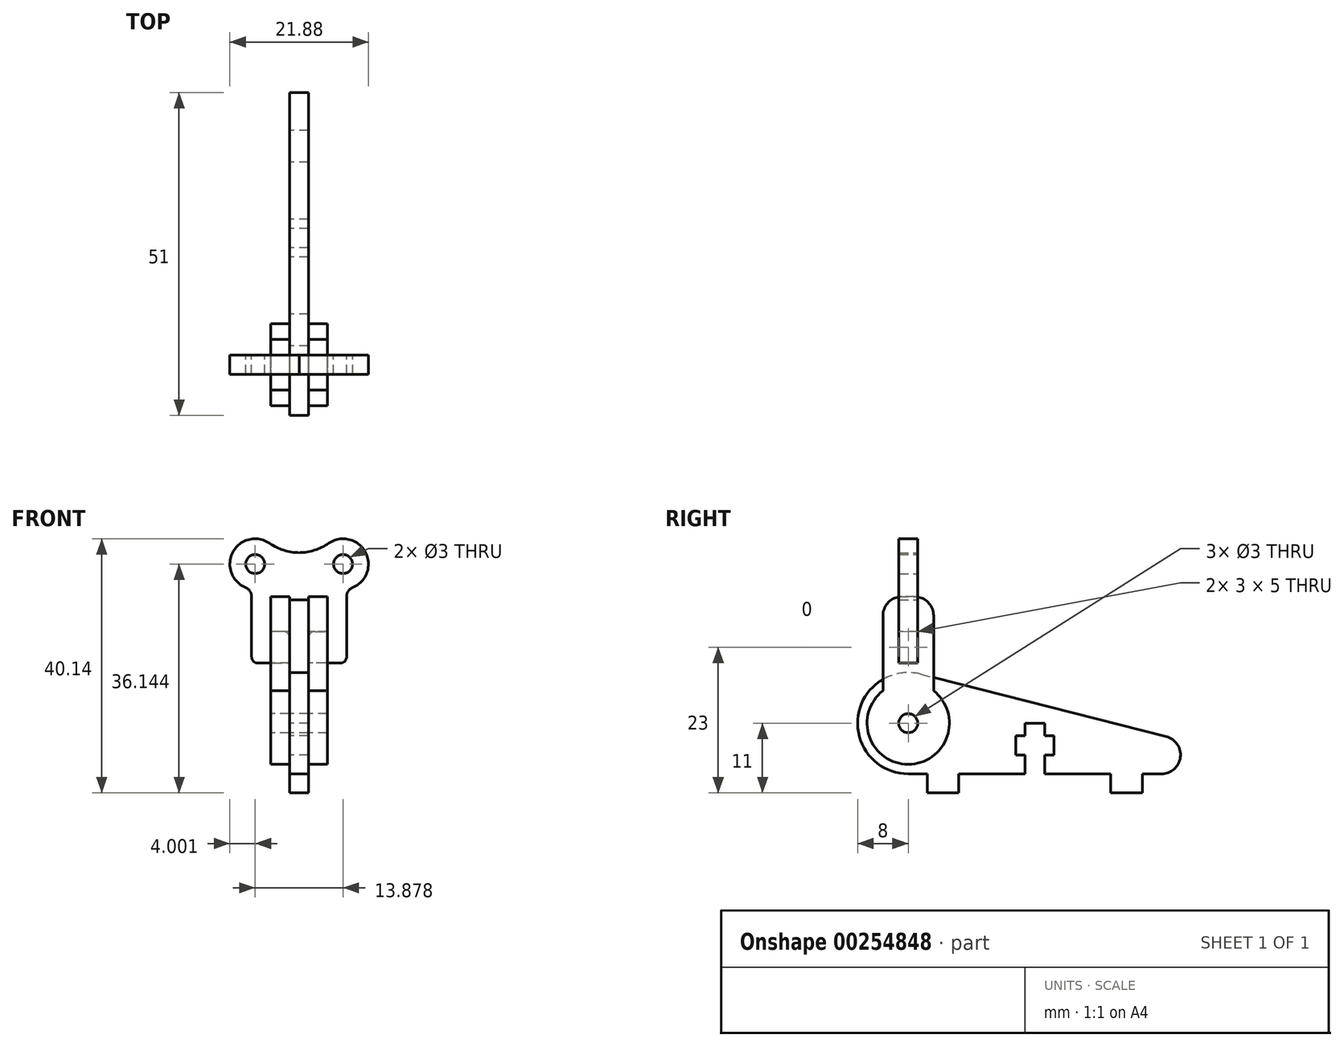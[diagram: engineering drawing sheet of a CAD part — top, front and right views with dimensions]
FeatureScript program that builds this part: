
annotation { "Feature Type Name" : "Feature", "Feature Type Description" : "" }
export const myFeature = defineFeature(function(context is Context, id is Id, definition is map)
    precondition{}
    {
        {
            var Q0;
            Q0=qCreatedBy(makeId("Right.planeOp"),FACE);
            var sketch = newSketch(context, id + "F0", { "sketchPlane" : qUnion([Q0])});
            skLineSegment(sketch, "E0", {"start": v(-20, 0) * mm, "end": v(-17, 0) * mm});
            skLineSegment(sketch, "E1", {"start": v(-17, 0) * mm, "end": v(-17, -3) * mm});
            skLineSegment(sketch, "E2", {"start": v(-17, -3) * mm, "end": v(-12, -3) * mm});
            skLineSegment(sketch, "E3", {"start": v(-12, -3) * mm, "end": v(-12, 0) * mm});
            skLineSegment(sketch, "E4", {"start": v(-12, 0) * mm, "end": v(-1.55, 0) * mm});
            skLineSegment(sketch, "E5", {"start": v(1.55, 0) * mm, "end": v(12, 0) * mm});
            skLineSegment(sketch, "E6", {"start": v(12, 0) * mm, "end": v(12, -3) * mm});
            skLineSegment(sketch, "E7", {"start": v(12, -3) * mm, "end": v(17, -3) * mm});
            skLineSegment(sketch, "E8", {"start": v(17, -3) * mm, "end": v(17, 0) * mm});
            skLineSegment(sketch, "E9", {"start": v(17, 0) * mm, "end": v(20, 0) * mm});
            skLineSegment(sketch, "E10", {"start": v(-1.55, 0) * mm, "end": v(-1.55, 3) * mm});
            skLineSegment(sketch, "E11", {"start": v(-1.55, 3) * mm, "end": v(-3, 3) * mm});
            skLineSegment(sketch, "E12", {"start": v(-3, 3) * mm, "end": v(-3, 6) * mm});
            skLineSegment(sketch, "E13", {"start": v(-3, 6) * mm, "end": v(-1.55, 6) * mm});
            skLineSegment(sketch, "E14", {"start": v(-1.55, 6) * mm, "end": v(-1.55, 8) * mm});
            skLineSegment(sketch, "E15", {"start": v(-1.55, 8) * mm, "end": v(1.55, 8) * mm});
            skLineSegment(sketch, "E16", {"start": v(1.55, 8) * mm, "end": v(1.55, 6) * mm});
            skLineSegment(sketch, "E17", {"start": v(1.55, 6) * mm, "end": v(3, 6) * mm});
            skLineSegment(sketch, "E18", {"start": v(3, 6) * mm, "end": v(3, 3) * mm});
            skLineSegment(sketch, "E19", {"start": v(3, 3) * mm, "end": v(1.55, 3) * mm});
            skLineSegment(sketch, "E20", {"start": v(1.55, 0) * mm, "end": v(1.55, 3) * mm});
            skArc(sketch, "E21", {"start": v(-20, 0) * mm, "mid": v(-27.94, 9) * mm, "end": v(-18.03, 15.75) * mm});
            skCircle(sketch, "E22", {"center": v(-20, 8) * mm, "radius": 1.5 * mm});
            skArc(sketch, "E23", {"start": v(20, 0) * mm, "mid": v(22.98, 2.63) * mm, "end": v(20.74, 5.9) * mm});
            skLineSegment(sketch, "E24", {"start": v(-18.03, 15.75) * mm, "end": v(20.74, 5.9) * mm});
            skSolve(sketch);
        }
        {
            var Q0;
            Q0 = qSketchRegion(id + "F0", true);
            extrude(context, id + "F1", {"entities" : qUnion([Q0]), "depth" : 3 * mm, "symmetric" : true});
        }
        {
            var Q0;
            Q0=makeQuery(id+"F1.opExtrude","CAP_FACE",FACE,{"disambiguationData":[OSD([sQuery(id+"F0.wireOp",EDGE,"E0"),sQuery(id+"F0.wireOp",EDGE,"E1"),sQuery(id+"F0.wireOp",EDGE,"E2"),sQuery(id+"F0.wireOp",EDGE,"E3"),sQuery(id+"F0.wireOp",EDGE,"E4"),sQuery(id+"F0.wireOp",EDGE,"E5"),sQuery(id+"F0.wireOp",EDGE,"E6"),sQuery(id+"F0.wireOp",EDGE,"E7"),sQuery(id+"F0.wireOp",EDGE,"E8"),sQuery(id+"F0.wireOp",EDGE,"E9"),sQuery(id+"F0.wireOp",EDGE,"E10"),sQuery(id+"F0.wireOp",EDGE,"E11"),sQuery(id+"F0.wireOp",EDGE,"E12"),sQuery(id+"F0.wireOp",EDGE,"E13"),sQuery(id+"F0.wireOp",EDGE,"E14"),sQuery(id+"F0.wireOp",EDGE,"E15"),sQuery(id+"F0.wireOp",EDGE,"E16"),sQuery(id+"F0.wireOp",EDGE,"E17"),sQuery(id+"F0.wireOp",EDGE,"E18"),sQuery(id+"F0.wireOp",EDGE,"E19"),sQuery(id+"F0.wireOp",EDGE,"E20"),sQuery(id+"F0.wireOp",EDGE,"E21"),sQuery(id+"F0.wireOp",EDGE,"E22"),sQuery(id+"F0.wireOp",EDGE,"E23"),sQuery(id+"F0.wireOp",EDGE,"E24")])],"isStart":false});
            var sketch = newSketch(context, id + "F2", { "sketchPlane" : qUnion([Q0])});
            skCircle(sketch, "E25", {"center": v(-20, 8) * mm, "radius": 1.5 * mm});
            skArc(sketch, "E26.0", {"start": v(-24, 13.12) * mm, "mid": v(-20, 1.5) * mm, "end": v(-16, 13.12) * mm});
            skLineSegment(sketch, "E27", {"start": v(-20, 24.79) * mm, "end": v(-20, -12.76) * mm, "construction": true});
            skLineSegment(sketch, "E28.top", {"start": v(-19, 28) * mm, "end": v(-21, 28) * mm});
            skLineSegment(sketch, "E28.left", {"start": v(-16, 13.12) * mm, "end": v(-16, 25) * mm});
            skLineSegment(sketch, "E28.right", {"start": v(-24, 13.12) * mm, "end": v(-24, 25) * mm});
            skPoint(sketch, "E28.middle", {"position": v(-20, 20.56) * mm});
            skLineSegment(sketch, "E29.bottom", {"start": v(-18.5, 17.5) * mm, "end": v(-21.5, 17.5) * mm});
            skLineSegment(sketch, "E29.top", {"start": v(-18.5, 22.5) * mm, "end": v(-21.5, 22.5) * mm});
            skLineSegment(sketch, "E29.left", {"start": v(-18.5, 17.5) * mm, "end": v(-18.5, 22.5) * mm});
            skLineSegment(sketch, "E29.right", {"start": v(-21.5, 17.5) * mm, "end": v(-21.5, 22.5) * mm});
            skPoint(sketch, "E29.middle", {"position": v(-20, 20) * mm});
            skPoint(sketch, "E30.visualSharp", {"position": v(-24, 28) * mm});
            skArc(sketch, "E30.filletArc", {"start": v(-21, 28) * mm, "mid": v(-23.12, 27.12) * mm, "end": v(-24, 25) * mm});
            skPoint(sketch, "E31.visualSharp", {"position": v(-16, 28) * mm});
            skArc(sketch, "E31.filletArc", {"start": v(-16, 25) * mm, "mid": v(-16.88, 27.12) * mm, "end": v(-19, 28) * mm});
            skSolve(sketch);
        }
        {
            var Q0;
            Q0 = qSketchRegion(id + "F2", true);
            extrude(context, id + "F3", {"entities" : qUnion([Q0]), "depth" : 3 * mm});
        }
        {
            var Q0;
            Q0=makeQuery(id+"F3.opExtrude","SWEPT_BODY",BODY,{"disambiguationData":[OSD([sQuery(id+"F2.wireOp",EDGE,"E25"),sQuery(id+"F2.wireOp",EDGE,"E26.0"),sQuery(id+"F2.wireOp",EDGE,"E28.top"),sQuery(id+"F2.wireOp",EDGE,"E28.left"),sQuery(id+"F2.wireOp",EDGE,"E28.right"),sQuery(id+"F2.wireOp",EDGE,"E29.bottom"),sQuery(id+"F2.wireOp",EDGE,"E29.top"),sQuery(id+"F2.wireOp",EDGE,"E29.left"),sQuery(id+"F2.wireOp",EDGE,"E29.right"),sQuery(id+"F2.wireOp",EDGE,"E30.filletArc"),sQuery(id+"F2.wireOp",EDGE,"E31.filletArc")])]});
            transform(context, id + "F4", {"entities" : qUnion([Q0]), "transformType" : TransformType.TRANSLATION_3D, "dx" : -6 * mm, "dy" : 0 * mm, "dz" : 0 * mm, "makeCopy" : true});
        }
        {
            var Q0;
            Q0=makeQuery(id+"F3.opExtrude","SWEPT_FACE",FACE,{"disambiguationData":[OSD([sQuery(id+"F2.wireOp",EDGE,"E29.left")])]});
            var Q1;
            Q1=makeQuery(id+"F3.opExtrude","SWEPT_FACE",FACE,{"disambiguationData":[OSD([sQuery(id+"F2.wireOp",EDGE,"E29.right")])]});
            cPlane(context, id + "F5", {"entities" : qUnion([Q0, Q1]), "cplaneType" : CPlaneType.MID_PLANE, "offset" : 25 * mm, "width" : 150 * mm, "height" : 150 * mm});
        }
        {
            var Q0;
            Q0=qCreatedBy(id+"F5.planeOp",FACE);
            var sketch = newSketch(context, id + "F6", { "sketchPlane" : qUnion([Q0])});
            skLineSegment(sketch, "E32", {"start": v(0, 27.5) * mm, "end": v(-1.5, 27.5) * mm});
            skLineSegment(sketch, "E33", {"start": v(-1.5, 27.5) * mm, "end": v(-1.5, 28) * mm});
            skLineSegment(sketch, "E34", {"start": v(-1.5, 28) * mm, "end": v(-4.5, 28) * mm});
            skLineSegment(sketch, "E35", {"start": v(-7.5, 18.5) * mm, "end": v(-7.5, 28) * mm});
            skArc(sketch, "E36", {"start": v(-7.5, 28) * mm, "mid": v(-7.76, 28.87) * mm, "end": v(-8.47, 29.45) * mm});
            skArc(sketch, "E37", {"start": v(-8.47, 29.45) * mm, "mid": v(-10.45, 35.05) * mm, "end": v(-4.67, 36.44) * mm});
            skCircle(sketch, "E38", {"center": v(-6.94, 33.14) * mm, "radius": 1.5 * mm});
            skLineSegment(sketch, "E39", {"start": v(-6.5, 17.5) * mm, "end": v(-1.5, 17.5) * mm});
            skLineSegment(sketch, "E40", {"start": v(-1.5, 17.5) * mm, "end": v(-1.5, 21.5) * mm});
            skLineSegment(sketch, "E41", {"start": v(-2.5, 22.5) * mm, "end": v(-4.5, 22.5) * mm});
            skLineSegment(sketch, "E42", {"start": v(-4.5, 22.5) * mm, "end": v(-4.5, 28) * mm});
            skPoint(sketch, "E43.visualSharp", {"position": v(-7.5, 17.5) * mm});
            skArc(sketch, "E43.filletArc", {"start": v(-7.5, 18.5) * mm, "mid": v(-7.2, 17.8) * mm, "end": v(-6.5, 17.5) * mm});
            skArc(sketch, "E44", {"start": v(-4.67, 36.44) * mm, "mid": v(-2.44, 35.34) * mm, "end": v(0, 34.94) * mm});
            skArc(sketch, "E45.MirrorCS", {"start": v(4.67, 36.44) * mm, "mid": v(2.44, 35.34) * mm, "end": v(0, 34.94) * mm});
            skArc(sketch, "E46.MirrorCS", {"start": v(8.47, 29.45) * mm, "mid": v(10.45, 35.05) * mm, "end": v(4.67, 36.44) * mm});
            skCircle(sketch, "E47.MirrorC", {"center": v(6.94, 33.14) * mm, "radius": 1.5 * mm});
            skArc(sketch, "E48.MirrorCS", {"start": v(7.5, 28) * mm, "mid": v(7.76, 28.87) * mm, "end": v(8.47, 29.45) * mm});
            skLineSegment(sketch, "E49.MirrorCS", {"start": v(7.5, 18.5) * mm, "end": v(7.5, 28) * mm});
            skArc(sketch, "E50.MirrorCS", {"start": v(7.5, 18.5) * mm, "mid": v(7.2, 17.8) * mm, "end": v(6.5, 17.5) * mm});
            skLineSegment(sketch, "E51.MirrorCS", {"start": v(6.5, 17.5) * mm, "end": v(1.5, 17.5) * mm});
            skLineSegment(sketch, "E52.MirrorCS", {"start": v(1.5, 17.5) * mm, "end": v(1.5, 21.5) * mm});
            skLineSegment(sketch, "E53.MirrorCS", {"start": v(2.5, 22.5) * mm, "end": v(4.5, 22.5) * mm});
            skLineSegment(sketch, "E54.MirrorCS", {"start": v(4.5, 22.5) * mm, "end": v(4.5, 28) * mm});
            skLineSegment(sketch, "E55.MirrorCS", {"start": v(1.5, 28) * mm, "end": v(4.5, 28) * mm});
            skLineSegment(sketch, "E56.MirrorCS", {"start": v(1.5, 27.5) * mm, "end": v(1.5, 28) * mm});
            skLineSegment(sketch, "E57.MirrorCS", {"start": v(0, 27.5) * mm, "end": v(1.5, 27.5) * mm});
            skPoint(sketch, "E58.visualSharp", {"position": v(-1.5, 22.5) * mm});
            skArc(sketch, "E58.filletArc", {"start": v(-1.5, 21.5) * mm, "mid": v(-1.8, 22.2) * mm, "end": v(-2.5, 22.5) * mm});
            skPoint(sketch, "E59.visualSharp", {"position": v(1.5, 22.5) * mm});
            skArc(sketch, "E59.filletArc", {"start": v(2.5, 22.5) * mm, "mid": v(1.8, 22.2) * mm, "end": v(1.5, 21.5) * mm});
            skSolve(sketch);
        }
        {
            var Q0;
            Q0 = qSketchRegion(id + "F6", true);
            extrude(context, id + "F7", {"entities" : qUnion([Q0]), "depth" : 3 * mm, "symmetric" : true});
        }
    });
